# Revit family: RN 81042 Optipress-Aquaplus-Vis de rappel isolante
name_source: partatom
category: Rohrformteile
units: mm (PartAtom-declared; Revit-internal decimal feet)

## family parameters
Arbeitsebenenbasiert = Nein
Beim Laden mit Abzugskörper schneiden = Nein
Bemaßung runder Anschluss = Durchmesser verwenden
Gemeinsam genutzt = Nein
Immer vertikal = Ja
Teiletyp = Verbindung

## types (10) — shared parameters
1.010.00.2 Numéro de feuille de la directive = 29
1.010.00.3 Date de publication (mois) de la ligne directrice = 201308
1.010.00.4 Nom du Fabricant = R. Nussbaum AG
1.010.00.5 Date de révision du fichier = 20190521
1.010.00.6 Adresse Web du fabricant = http://www.nussbaum.ch
1.100.00.4 Désignation du produit = Alimentation
1.110.00.2 Indice = 4
1.110.00.4 Désignation du produit = Optipress
1.960/3L.00.8 Lien (URL) = https://www.nussbaum.ch
29.700.00.4 Nom du produit = Optipress-A-Vis de rappel isolante, avec filetage femelle
29.700.00.5 Identification du produit = 2
29.700.00.6 Forme transversale = 1
29.700.00.7 Système de taille nominale = DN
29.700.00.8 Système de pression nominale = PN
29.710.02.4 Pression nominale = 16
29.710.02.5 Max. [hPa] = 1600
29.710.02.7 Max. [hPa] = 1600
29.710.02.9 Max. [°C] = 95
Connector Visibility = Nein
EnclosingSpace Visibility = Nein

## per-type parameters (varying)
| type | 1.800.00.3 Numéro BS | 1.810.00.3 Numéro de commande fabricant | 1.810.00.4 Numéro DATANORM | 1.810.00.5 Numéro StLB | 1.810.00.6 Numéro GTIN | 29.710.02.10 Poids d'ajustement [kg] | 29.710.02.3 La désignation | CONNECTOR0_DIAMETER_dX_0r | CONNECTOR0_dX_01 | CONNECTOR0_ref_dX | CONNECTOR1_DIAMETER_dX_0r | CONNECTOR1_dX_00 | CONNECTOR1_dX_01 | CONNECTOR1_ref_dX | R. Nussbaum AG 81042.21 fr Visibility | R. Nussbaum AG 81042.22 fr Visibility | R. Nussbaum AG 81042.23 fr Visibility | R. Nussbaum AG 81042.24 fr Visibility | R. Nussbaum AG 81042.25 fr Visibility | R. Nussbaum AG 81042.26 fr Visibility | R. Nussbaum AG 81042.27 fr Visibility | R. Nussbaum AG 81042.28 fr Visibility | R. Nussbaum AG 81042.29 fr Visibility | R. Nussbaum AG 81042.30 fr Visibility |
| 81042.21, Optipress-A-Vis de rappel isolante, avec filetage femelle, DN=12x15, L=55, Rp=½ | 01900400000000000000000000000000000000000000000042000000000000000001 | 81042.21 | 81042.21 | 284.413 | 7612945672421 | 0.184 | Optipress-A-Vis de rappel isolante, avec filetage femelle, DN=12x15, L=55, Rp=½ | 12 mm  [stored 0.0393701 ft] | 22 mm  [stored 0.0721785 ft] | 22 mm  [stored 0.0721785 ft] | 15 mm | 42 mm | 55 mm | 42 mm | Ja | Nein | Nein | Nein | Nein | Nein | Nein | Nein | Nein | Nein |
| 81042.22, Optipress-A-Vis de rappel isolante, avec filetage femelle, DN=15x20, L=64, Rp=¾ | 01900400000000000000000000000000000000000000000042000000000000000002 | 81042.22 | 81042.22 | 284.412 | 7612945672438 | 0.198 | Optipress-A-Vis de rappel isolante, avec filetage femelle, DN=15x20, L=64, Rp=¾ | 12 mm  [stored 0.0393701 ft] | 22 mm  [stored 0.0721785 ft] | 22 mm  [stored 0.0721785 ft] | 20 mm  [stored 0.0656168 ft] | 49 mm | 64 mm | 49 mm | Nein | Ja | Nein | Nein | Nein | Nein | Nein | Nein | Nein | Nein |
| 81042.23, Optipress-A-Vis de rappel isolante, avec filetage femelle, DN=15, L=58, Rp=½ | 01900400000000000000000000000000000000000000000042000000000000000003 | 81042.23 | 81042.23 | 284.413 | 7612945672445 | 0.334 | Optipress-A-Vis de rappel isolante, avec filetage femelle, DN=15, L=58, Rp=½ | 15 mm | 22 mm  [stored 0.0721785 ft] | 22 mm  [stored 0.0721785 ft] | 15 mm | 45 mm | 58 mm | 45 mm | Nein | Nein | Ja | Nein | Nein | Nein | Nein | Nein | Nein | Nein |
| 81042.24, Optipress-A-Vis de rappel isolante, avec filetage femelle, DN=15x20, L=58, Rp=¾ | 01900400000000000000000000000000000000000000000042000000000000000004 | 81042.24 | 81042.24 | 284.413 | 7612945672452 | 0.31 | Optipress-A-Vis de rappel isolante, avec filetage femelle, DN=15x20, L=58, Rp=¾ | 15 mm | 22 mm  [stored 0.0721785 ft] | 22 mm  [stored 0.0721785 ft] | 20 mm  [stored 0.0656168 ft] | 43 mm | 58 mm | 43 mm | Nein | Nein | Nein | Ja | Nein | Nein | Nein | Nein | Nein | Nein |
| 81042.25, Optipress-A-Vis de rappel isolante, avec filetage femelle, DN=20, L=63, Rp=¾ | 01900400000000000000000000000000000000000000000042000000000000000005 | 81042.25 | 81042.25 | 284.414 | 7612945672469 | 0.484 | Optipress-A-Vis de rappel isolante, avec filetage femelle, DN=20, L=63, Rp=¾ | 20 mm  [stored 0.0656168 ft] | 24 mm | 24 mm | 20 mm  [stored 0.0656168 ft] | 48 mm | 63 mm | 48 mm | Nein | Nein | Nein | Nein | Ja | Nein | Nein | Nein | Nein | Nein |
| 81042.26, Optipress-A-Vis de rappel isolante, avec filetage femelle, DN=20x25, L=65, Rp=1 | 01900400000000000000000000000000000000000000000042000000000000000006 | 81042.26 | 81042.26 | 284.414 | 7612945672476 | 0.476 | Optipress-A-Vis de rappel isolante, avec filetage femelle, DN=20x25, L=65, Rp=1 | 20 mm  [stored 0.0656168 ft] | 24 mm | 24 mm | 25 mm  [stored 0.082021 ft] | 48 mm | 65 mm | 48 mm | Nein | Nein | Nein | Nein | Nein | Ja | Nein | Nein | Nein | Nein |
| 81042.27, Optipress-A-Vis de rappel isolante, avec filetage femelle, DN=25, L=65, Rp=1 | 01900400000000000000000000000000000000000000000042000000000000000007 | 81042.27 | 81042.27 | 284.415 | 7612945672483 | 0.46 | Optipress-A-Vis de rappel isolante, avec filetage femelle, DN=25, L=65, Rp=1 | 25 mm  [stored 0.082021 ft] | 24 mm | 24 mm | 25 mm  [stored 0.082021 ft] | 48 mm | 65 mm | 48 mm | Nein | Nein | Nein | Nein | Nein | Nein | Ja | Nein | Nein | Nein |
| 81042.28, Optipress-A-Vis de rappel isolante, avec filetage femelle, DN=32, L=68, Rp=1¼ | 01900400000000000000000000000000000000000000000042000000000000000008 | 81042.28 | 81042.28 | 284.416 | 7612945672490 | 0.78 | Optipress-A-Vis de rappel isolante, avec filetage femelle, DN=32, L=68, Rp=1¼ | 32 mm | 26 mm | 26 mm | 32 mm | 49 mm | 68 mm | 49 mm | Nein | Nein | Nein | Nein | Nein | Nein | Nein | Ja | Nein | Nein |
| 81042.29, Optipress-A-Vis de rappel isolante, avec filetage femelle, DN=40, L=77, Rp=1½ | 01900400000000000000000000000000000000000000000042000000000000000009 | 81042.29 | 81042.29 | 284.417 | 7612945672506 | 0.89 | Optipress-A-Vis de rappel isolante, avec filetage femelle, DN=40, L=77, Rp=1½ | 40 mm | 36 mm | 36 mm | 40 mm | 58 mm | 77 mm | 58 mm | Nein | Nein | Nein | Nein | Nein | Nein | Nein | Nein | Ja | Nein |
| 81042.30, Optipress-A-Vis de rappel isolante, avec filetage femelle, DN=50, L=90, Rp=2 | 01900400000000000000000000000000000000000000000042000000000000000010 | 81042.30 | 81042.30 | 284.417 | 7612945672513 | 1.37 | Optipress-A-Vis de rappel isolante, avec filetage femelle, DN=50, L=90, Rp=2 | 50 mm | 40 mm | 40 mm | 50 mm | 66 mm | 90 mm | 66 mm | Nein | Nein | Nein | Nein | Nein | Nein | Nein | Nein | Nein | Ja |

note: column(s) folded — value = type name in every type: 1.800.00.4 Champ de commentaires

note: [stored X ft] marks values corroborated as IEEE doubles in the binary element streams (Revit-internal decimal feet)

## geometry (parser evidence)
native form markers: Sweep x3
no freeform markers — native parametric forms only
